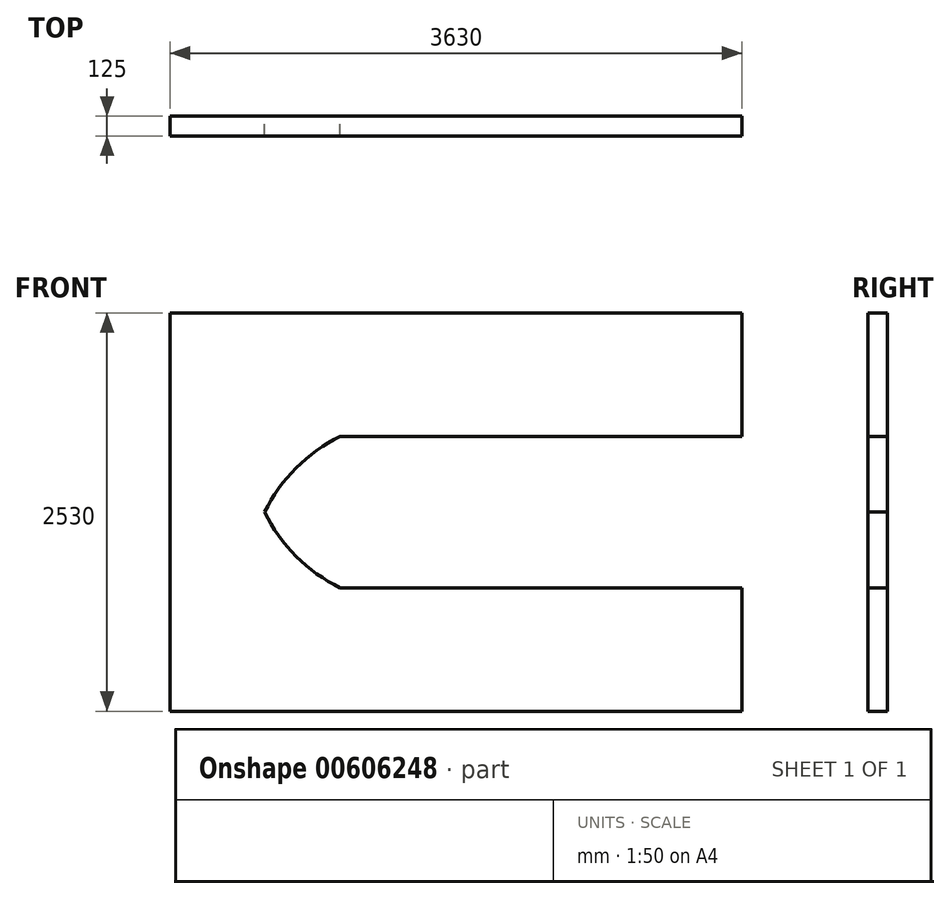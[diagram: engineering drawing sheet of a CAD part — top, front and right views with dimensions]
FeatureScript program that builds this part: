
annotation { "Feature Type Name" : "Feature", "Feature Type Description" : "" }
export const myFeature = defineFeature(function(context is Context, id is Id, definition is map)
    precondition{}
    {
        {
            var Q0;
            Q0=qCreatedBy(makeId("Front.planeOp"),FACE);
            var sketch = newSketch(context, id + "F0", { "sketchPlane" : qUnion([Q0])});
            skLineSegment(sketch, "E0.bottom", {"start": v(-1792.9, 183.5) * mm, "end": v(1837.1, 183.5) * mm});
            skLineSegment(sketch, "E0.top", {"start": v(-1792.9, -1081.5) * mm, "end": v(1837.1, -1081.5) * mm});
            skLineSegment(sketch, "E0.left", {"start": v(-1792.9, 183.5) * mm, "end": v(-1792.9, -1081.5) * mm});
            skLineSegment(sketch, "E0.right", {"start": v(1837.1, 183.5) * mm, "end": v(1837.1, -1081.5) * mm});
            skSolve(sketch);
        }
        {
            var Q0;
            Q0=makeQuery(id+"F0.imprint","IMPRINT",FACE,{"disambiguationData":[TD([[makeQuery(id+"F0.imprint","IMPRINT",EDGE,{"derivedFrom":sQuery(id+"F0.wireOp",EDGE,"E0.bottom")}),-1.0]])]});
            extrude(context, id + "F1", {"entities" : qUnion([Q0]), "depth" : 125 * mm, "offsetDistance" : 25 * mm});
        }
        {
            var Q0;
            Q0=makeQuery(id+"F1.opExtrude","CAP_FACE",FACE,{"disambiguationData":[OSD([sQuery(id+"F0.wireOp",EDGE,"E0.bottom"),sQuery(id+"F0.wireOp",EDGE,"E0.top"),sQuery(id+"F0.wireOp",EDGE,"E0.left"),sQuery(id+"F0.wireOp",EDGE,"E0.right")])],"isStart":true});
            var sketch = newSketch(context, id + "F2", { "sketchPlane" : qUnion([Q0])});
            skLineSegment(sketch, "E1", {"start": v(-1237.1, 183.5) * mm, "end": v(-757.1, -296.5) * mm});
            skLineSegment(sketch, "E2", {"start": v(712.9, -296.5) * mm, "end": v(1192.9, 183.5) * mm});
            skLineSegment(sketch, "E3", {"start": v(-757.1, -296.5) * mm, "end": v(712.9, -296.5) * mm});
            skLineSegment(sketch, "E4", {"start": v(-1237.1, 183.5) * mm, "end": v(1192.9, 183.5) * mm});
            skSolve(sketch);
        }
        {
            var Q0;
            Q0=qSketchRegion(id+"F2",true);
            extrude(context, id + "F3", {"entities" : qUnion([Q0]), "operationType" : NewBodyOperationType.REMOVE, "endBound" : BoundingType.UP_TO_NEXT, "oppositeDirection" : true, "depth" : 125 * mm, "offsetDistance" : 25 * mm});
        }
        {
            var Q0;
            Q0=makeQuery(id+"F1.opExtrude","CAP_FACE",FACE,{"disambiguationData":[OSD([sQuery(id+"F0.wireOp",EDGE,"E0.bottom"),sQuery(id+"F0.wireOp",EDGE,"E0.top"),sQuery(id+"F0.wireOp",EDGE,"E0.left"),sQuery(id+"F0.wireOp",EDGE,"E0.right")])],"isStart":false});
            var sketch = newSketch(context, id + "F4", { "sketchPlane" : qUnion([Q0])});
            skLineSegment(sketch, "E5", {"start": v(757.1, -296.5) * mm, "end": v(1237.1, 183.5) * mm});
            skLineSegment(sketch, "E6", {"start": v(1237.1, 183.5) * mm, "end": v(1837.1, 183.5) * mm});
            skLineSegment(sketch, "E7", {"start": v(1837.1, 183.5) * mm, "end": v(1837.1, -296.5) * mm});
            skLineSegment(sketch, "E8", {"start": v(1837.1, -296.5) * mm, "end": v(757.1, -296.5) * mm});
            skSolve(sketch);
        }
        {
            var Q0;
            Q0=makeQuery(id+"F4.imprint","IMPRINT",FACE,{"disambiguationData":[TD([[makeQuery(id+"F4.imprint","IMPRINT",EDGE,{"derivedFrom":sQuery(id+"F4.wireOp",EDGE,"E5")}),1.0]])]});
            extrude(context, id + "F5", {"entities" : qUnion([Q0]), "operationType" : NewBodyOperationType.REMOVE, "endBound" : BoundingType.UP_TO_NEXT, "oppositeDirection" : true, "depth" : 25 * mm, "offsetDistance" : 25 * mm});
        }
        {
            var Q0;
            Q0=makeQuery(id+"F1.opExtrude","CAP_FACE",FACE,{"disambiguationData":[OSD([sQuery(id+"F0.wireOp",EDGE,"E0.bottom"),sQuery(id+"F0.wireOp",EDGE,"E0.top"),sQuery(id+"F0.wireOp",EDGE,"E0.left"),sQuery(id+"F0.wireOp",EDGE,"E0.right")])],"isStart":false});
            var sketch = newSketch(context, id + "F6", { "sketchPlane" : qUnion([Q0])});
            skArc(sketch, "E9", {"start": v(-1192.9, 183.5) * mm, "mid": v(-993.47, -97.08) * mm, "end": v(-712.9, -296.5) * mm});
            skLineSegment(sketch, "E10", {"start": v(-1192.9, 183.5) * mm, "end": v(-712.9, -296.5) * mm});
            skSolve(sketch);
        }
        {
            var Q0;
            Q0=makeQuery(id+"F6.imprint","IMPRINT",FACE,{"disambiguationData":[TD([[makeQuery(id+"F6.imprint","IMPRINT",EDGE,{"derivedFrom":sQuery(id+"F6.wireOp",EDGE,"E9")}),1.0]])]});
            extrude(context, id + "F7", {"entities" : qUnion([Q0]), "operationType" : NewBodyOperationType.REMOVE, "endBound" : BoundingType.UP_TO_NEXT, "oppositeDirection" : true, "depth" : 25 * mm, "offsetDistance" : 25 * mm});
        }
        {
            var Q0;
            Q0=makeQuery(id+"F1.opExtrude","SWEPT_BODY",BODY,{"disambiguationData":[OSD([sQuery(id+"F0.wireOp",EDGE,"E0.bottom"),sQuery(id+"F0.wireOp",EDGE,"E0.top"),sQuery(id+"F0.wireOp",EDGE,"E0.left"),sQuery(id+"F0.wireOp",EDGE,"E0.right")])]});
            var Q1;
            {var subQ1=sQuery(id+"F0.wireOp",EDGE,"E0.left");var subQ3=sQuery(id+"F0.wireOp",EDGE,"E0.bottom");Q1=makeQuery(id+"F3.boolean.opBoolean","SPLIT",FACE,{"disambiguationData":[TD([makeQuery(id+"F1.opExtrude","SWEPT_FACE",FACE,{"disambiguationData":[OSD([subQ1])]})])],"derivedFrom":makeQuery(id+"F1.opExtrude","SWEPT_FACE",FACE,{"disambiguationData":[OSD([subQ3])]})});}
            mirror(context, id + "F8", {"operationType" : NewBodyOperationType.ADD, "entities" : qUnion([Q0]), "mirrorPlane" : qUnion([Q1])});
        }
    });
